# Revit family: Drain_Deck_Parking_9_Inch_Round_Top-Zurn-Z533-Heavy-Duty
name_source: partatom
category: Plumbing Fixtures
units: mm (PartAtom-declared; Revit-internal decimal feet)

## family parameters
Always vertical = Yes
Cut with Voids When Loaded = No
Maintain Annotation Orientation = No
OmniClass Number = 23.45.55.21
OmniClass Title = Drains (Wastes)
Part Type = Normal
Room Calculation Point = No
Round Connector Dimension = Use Radius
Shared = No
Work Plane-Based = No

## types (8) — shared parameters
Approx. Weight (Lbs) = 48 "
Assembly Code = D2030300
CW Connection = No
Default Elevation = 4 "
Description = 9 [229] DIAMETER HEAVY-DUTY PARKING DECK DRAIN W/ SUPPORT FLANGE
Grate Open Area (Sq. In) = 16
HW Connection = No
Main Material = Iron - Zurn - Cast - Painted - Blue
Manufacturer = Zurn Water, LLC
Manufacurer Brand = Zurn
Modified Date = 12/23/2025
Product Documentation Link = https://files.zurn.com
Product Page URL = https://www.zurn.com
Product data url = https://www.bimobject.com
Top Grate diameter = 8 "
Top diameter = 9 "
Trap Primer = Yes
URL = www.zurn.com
Vent Connection = No
Waste Connection = Yes
zero-valued in all types: CWFU, HWFU, WFU

## per-type parameters (varying)
| type | A_ Pipe Size (Actual-Inner) | A_ Pipe Size (Actual-Outer) | A_ Pipe Size (Nominal) | Connector Radius | E_ Body Height | Frame Height | Grate Material | Type Comments | ZN-Top |
| Z533-3NH | 3.068 " | 3.5 " | 3 " | 1.5 " | 5.25 " | 2 " | Iron - Zurn - Cast - Painted - Blue | Z533-3 Inch No-Hub Outlet | No |
| Z533-4NH | 4.026 " | 4.5 " | 4 " | 2 " | 5.25 " | 2 " | Iron - Zurn - Cast - Painted - Blue | Z533-4 Inch No-Hub Outlet | No |
| Z533-3NL | 3.068 " | 3.5 " | 3 " | 1.5 " | 4.563 " | 2 " | Iron - Zurn - Cast - Painted - Blue | Z533-3 Inch Neo-Loc Outlet | No |
| Z533-4NL | 4.026 " | 4.5 " | 4 " | 2 " | 4.563 " | 2 " | Iron - Zurn - Cast - Painted - Blue | Z533-4 Inch Neo-Loc Outlet | No |
| ZN533-3NH | 3.068 " | 3.5 " | 3 " | 1.5 " | 5.25 " | 2.188 " | Bronze - Zurn - Polished Nickel | ZN533-3 Inch No-Hub Outlet with Polished Nickel Bronze Top | Yes |
| ZN533-4NH | 4.026 " | 4.5 " | 4 " | 2 " | 5.25 " | 2.188 " | Bronze - Zurn - Polished Nickel | ZN533-4 Inch No-Hub Outlet with Polished Nickel Bronze Top | Yes |
| ZN533-3NL | 3.068 " | 3.5 " | 3 " | 1.5 " | 4.563 " | 2.188 " | Bronze - Zurn - Polished Nickel | ZN533-3 Inch Neo-Loc Outlet with Polished Nickel Bronze Top | Yes |
| ZN533-4NL | 4.026 " | 4.5 " | 4 " | 2 " | 4.563 " | 2.188 " | Bronze - Zurn - Polished Nickel | ZN533-4 Inch Neo-Loc Outlet with Polished Nickel Bronze Top | Yes |

note: column(s) folded — value = type name in every type: Model

## geometry (parser evidence)
native form markers: Sweep x5
no freeform markers — native parametric forms only
